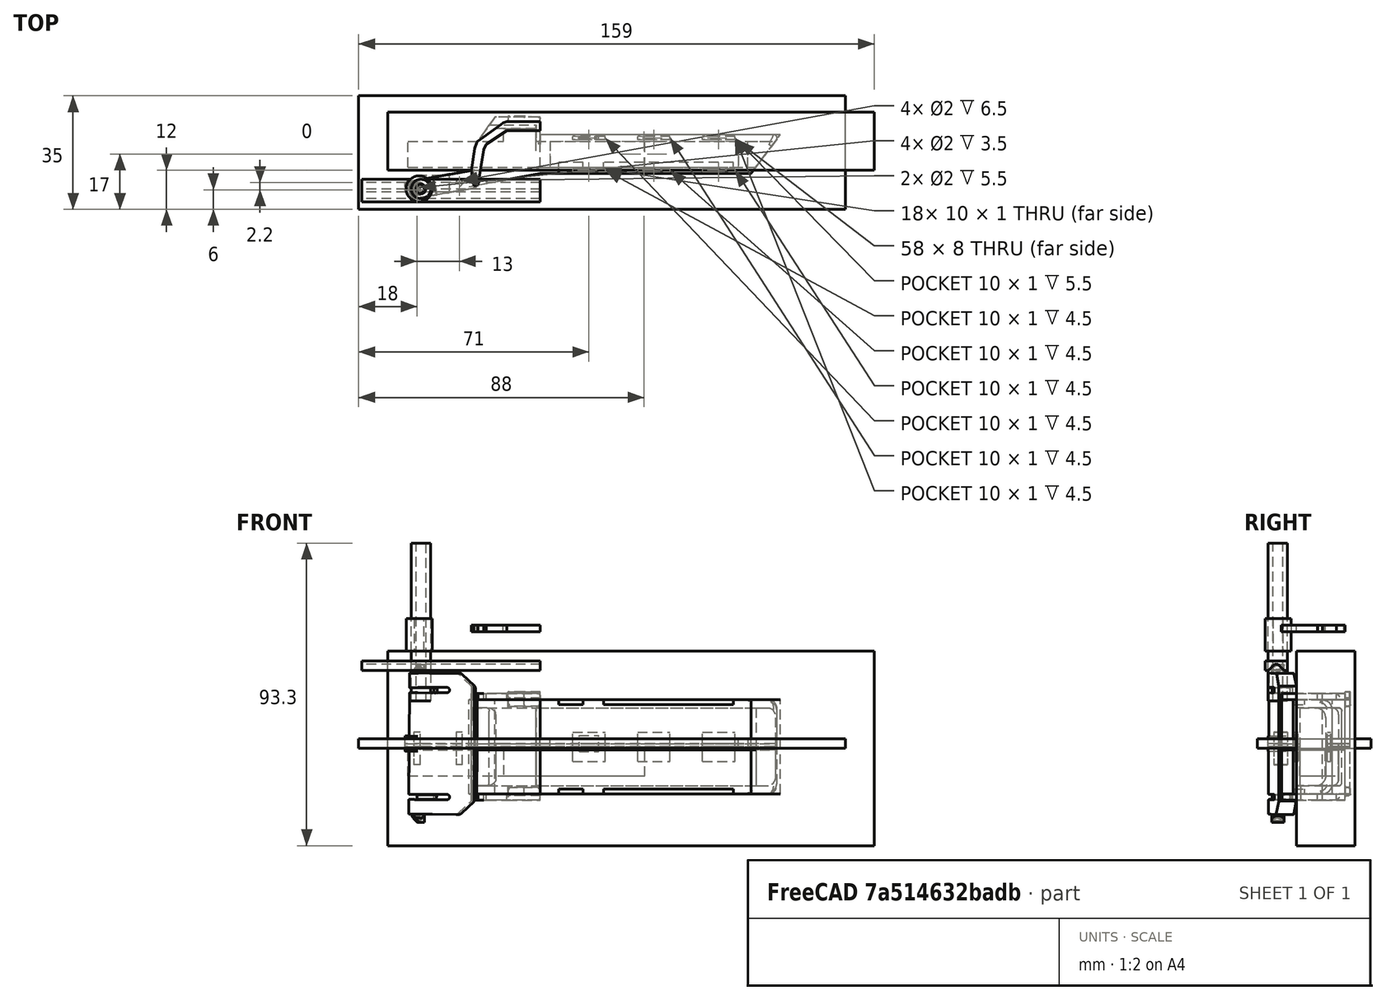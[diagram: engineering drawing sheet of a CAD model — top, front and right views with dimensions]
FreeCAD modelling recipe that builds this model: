
FCSTD DOCUMENT  (FreeCAD 0.21R33771 (Git))
Label: pieza_aspiradora
License: All rights reserved
LicenseURL: http://en.wikipedia.org/wiki/All_rights_reserved
objects: Part::Cut×69, Part::Box×57, Part::Fillet×31, Part::Feature×29, Part::Cylinder×14, Mesh::Feature×10, Sketcher::SketchObject×5, PartDesign::Pad×5, PartDesign::Body×5, Part::Chamfer×4, Part::MultiFuse×4, PartDesign::ShapeBinder×1, Part::Fuse×1
note: 230 computed .brp shape members not serialized (recipe doc carries the construction recipe); baked Part::Feature solids carry a one-line shape summary decoded from their .brp

FEATURE [Sketcher::SketchObject] Sketch
  FullyConstrained = true
  MapMode = 5
  sketch-geometry (8):
    g0: LineSegment StartX=0 StartY=0 StartZ=0 EndX=0 EndY=5.5 EndZ=0
    g1: LineSegment StartX=0 StartY=5.5 StartZ=0 EndX=-14 EndY=5.5 EndZ=0
    g2: LineSegment StartX=-14 StartY=5.5 StartZ=0 EndX=-20 EndY=-3 EndZ=0
    g3: LineSegment StartX=-20 StartY=-3 StartZ=0 EndX=-22 EndY=-16 EndZ=0
    g4: LineSegment StartX=-22 StartY=-16 StartZ=0 EndX=0 EndY=-12 EndZ=0
    g5: LineSegment StartX=0 StartY=-12 StartZ=0 EndX=65 EndY=-12 EndZ=0
    g6: LineSegment StartX=65 StartY=-12 StartZ=0 EndX=74 EndY=0 EndZ=0
    g7: LineSegment StartX=74 StartY=0 StartZ=0 EndX=0 EndY=0 EndZ=0
  constraints (24):
    c: PointOnObject(g0,g-1)
    c: PointOnObject(g0,g-2)
    c: Vertical(g0)
    c: Coincident(g0,g1)
    c: Coincident(g1,g2)
    c: Coincident(g2,g3)
    c: Coincident(g3,g4)
    c: Coincident(g4,g5)
    c: Horizontal(g5)
    c: Coincident(g5,g6)
    c: PointOnObject(g6,g-1)
    c: Coincident(g6,g7)
    c: Coincident(g7,g0)
    c: DistanceX(g7,g7) = 74
    c: DistanceX(g0,g4) = 0
    c: DistanceY(g0,g0) = 5.5
    c: Horizontal(g1)
    c: DistanceX(g1,g1) = 14
    c: DistanceX(g3,g-1) = 22
    c: DistanceX(g2,g0) = 20
    c: DistanceY(g3,g2) = 13
    c: DistanceX(g5,g5) = 65
    c: DistanceY(g5,g6) = 12
    c: DistanceY(g3,g4) = 4
FEATURE [PartDesign::Pad] Pad
  Direction = (0,0,1)
  Length = 29
  Length2 = 10
  Profile = -> Sketch
  ReferenceAxis = -> Sketch [N_Axis]
  Type = 0
FEATURE [Part::Feature] Body001
  shape: bbox 96 x 21.5 x 29 mm, 10 faces (baked)
FEATURE [Part::Fillet] Fillet
  Base = -> Body001
  Edges = 1 edges r=5: [Edge8]
FEATURE [Part::Fillet] Fillet001
  Base = -> Fillet
  Edges = 1 edges r=1: [Edge2]
FEATURE [Part::Fillet] Fillet002
  Base = -> Fillet001
  Edges = 1 edges r=3: [Edge22]
FEATURE [Part::Fillet] Fillet003
  Base = -> Fillet002
  Edges = 1 edges r=3: [Edge34]
FEATURE [Part::Fillet] Fillet004
  Base = -> Fillet003
  Edges = 6 edges r=1: [Edge1,Edge2,Edge3,Edge4,Edge5,Edge6]
FEATURE [Part::Box] Box  label="Cube"
  AttacherType = Attacher::AttachEngine3D
  Height = 24
  Length = 156
  Width = 8
FEATURE [Part::Fillet] Fillet005
  Base = -> Box
  Edges = 2 edges r=3: [Edge11,Edge12]
  Placement = pos=(-30,-10,2.5) rot=(0,0,1;0rad)
FEATURE [Part::Box] Box001  label="Cube001"
  AttacherType = Attacher::AttachEngine3D
  Height = 24
  Length = 28
  Placement = pos=(-29.3,-11,2.5) rot=(0,0,1;0rad)
  Width = 14
FEATURE [Part::Cut] Cut
  Base = -> Fillet004
  Tool = -> Fillet005
FEATURE [Part::Cut] Cut001
  Base = -> Cut
  Tool = -> Box001
FEATURE [Part::Chamfer] Chamfer
  Base = -> Cut001
  Edges = 1 edges r=0.95: [Edge38]
FEATURE [Part::Fillet] Fillet006
  Base = -> Chamfer
  Edges = 2 edges r=1: [Edge63,Edge91]
FEATURE [Part::Box] Box002  label="Cube002"
  AttacherType = Attacher::AttachEngine3D
  Height = 10
  Length = 40
  Placement = pos=(19.5,-12,-8.5) rot=(0,0,1;0rad)
  Width = 3.5
FEATURE [Part::Box] Box003  label="Cube003"
  AttacherType = Attacher::AttachEngine3D
  Height = 10
  Length = 40
  Placement = pos=(19.5,-12,27.5) rot=(0,0,1;0rad)
  Width = 3.5
FEATURE [Part::Box] Box005  label="Cube005"
  AttacherType = Attacher::AttachEngine3D
  Height = 10
  Length = 7.4
  Placement = pos=(5.7,-12,27.5) rot=(0,0,1;0rad)
  Width = 3.5
FEATURE [Part::Cut] Cut002
  Base = -> Fillet006
  Tool = -> Box002
FEATURE [Part::Cut] Cut003
  Base = -> Cut002
  Tool = -> Box003
FEATURE [Part::Box] Box006  label="Cube006"
  AttacherType = Attacher::AttachEngine3D
  Height = 10
  Length = 7.4
  Placement = pos=(5.7,-12,-8.5) rot=(0,0,1;0rad)
  Width = 3.5
FEATURE [Part::Cut] Cut004
  Base = -> Cut003
  Tool = -> Box005
FEATURE [Part::Cut] Cut005
  Base = -> Cut004
  Tool = -> Box006
FEATURE [Part::Box] Box007  label="Cube007"
  AttacherType = Attacher::AttachEngine3D
  Height = 30
  Length = 133
  Placement = pos=(-51,-22,14.5) rot=(0,0,1;0rad)
  Width = 30
FEATURE [Part::Box] Box008  label="Cube008"
  AttacherType = Attacher::AttachEngine3D
  Height = 30
  Length = 133
  Placement = pos=(-51,-22,-15.5) rot=(0,0,1;0rad)
  Width = 30
FEATURE [Part::Feature] Fillet003004001  label="pieza2_solida2"
  Placement = pos=(-31.9,-18.5,15.45) rot=(-0.059649,0.705848,0.705848;3.26865rad)
  shape: bbox 21.78 x 8.705 x 48.62 mm, 40 faces (baked)
FEATURE [Part::MultiFuse] Fusion
  Refine = true
  Shapes = -> [Cut005,Fillet003004001]
FEATURE [Part::Feature] Fusion001
  shape: bbox 114.9 x 25.2 x 48.62 mm, 92 faces (baked)
FEATURE [Part::Feature] Fusion002
  shape: bbox 114.9 x 25.2 x 48.62 mm, 92 faces (baked)
FEATURE [Part::Cut] Cut006
  Base = -> Fusion001
  Refine = true
  Tool = -> Box007
FEATURE [Part::Cut] Cut007
  Base = -> Fusion002
  Refine = true
  Tool = -> Box008
FEATURE [Part::Chamfer] Chamfer001  label="mitad1"
  Base = -> Cut006
  Edges = 1 edges r=0.72: [Edge121]
FEATURE [Part::Chamfer] Chamfer002  label="mitad2"
  Base = -> Cut007
  Edges = 1 edges r=0.72: [Edge127]
FEATURE [Part::Chamfer] Chamfer003  label="entera"
  Base = -> Fusion
  Edges = 1 edges r=0.72: [Edge141]
FEATURE [Part::Fillet] Fillet003004002  label="entire_solid2"
  Base = -> Chamfer003
  Edges = 4 edges r=0.7: [Edge20,Edge21,Edge46,Edge47]
FEATURE [Part::Fillet] Fillet003004003
  Base = -> Chamfer002
  Edges = 2 edges r=0.7: [Edge20,Edge21]
FEATURE [Part::Fillet] Fillet003004004
  Base = -> Chamfer001
  Edges = 2 edges r=0.7: [Edge20,Edge21]
FEATURE [Part::Box] Box009  label="Cube009"
  AttacherType = Attacher::AttachEngine3D
  Height = 9
  Length = 10
  Placement = pos=(30,-1.5,10) rot=(0,0,1;0rad)
  Width = 1
FEATURE [Part::Box] Box010  label="Cube010"
  AttacherType = Attacher::AttachEngine3D
  Height = 9
  Length = 10
  Placement = pos=(30,-1.5,10) rot=(0,0,1;0rad)
  Width = 1
FEATURE [Part::Box] Box011  label="Cube011"
  AttacherType = Attacher::AttachEngine3D
  Height = 9
  Length = 10
  Placement = pos=(10,-1.5,10) rot=(0,0,1;0rad)
  Width = 1
FEATURE [Part::Box] Box012  label="Cube012"
  AttacherType = Attacher::AttachEngine3D
  Height = 9
  Length = 10
  Placement = pos=(10,-11.5,10) rot=(0,0,1;0rad)
  Width = 1
FEATURE [Part::Box] Box013  label="Cube013"
  AttacherType = Attacher::AttachEngine3D
  Height = 9
  Length = 10
  Placement = pos=(30,-11.5,10) rot=(0,0,1;0rad)
  Width = 1
FEATURE [Part::Box] Box014  label="Cube014"
  AttacherType = Attacher::AttachEngine3D
  Height = 9
  Length = 10
  Placement = pos=(50,-11.5,10) rot=(0,0,1;0rad)
  Width = 1
FEATURE [Part::Feature] Fillet003004002001  label="entire"
  shape: bbox 114.9 x 25.2 x 48.62 mm, 97 faces (baked)
FEATURE [Part::Feature] Fillet003004003001  label="left2"
  shape: bbox 114.9 x 25.2 x 25.31 mm, 64 faces (baked)
FEATURE [Part::Feature] Fillet003004004001  label="right2"
  shape: bbox 114.9 x 25.2 x 23.35 mm, 62 faces (baked)
FEATURE [Part::Box] Box027  label="Cube027"
  AttacherType = Attacher::AttachEngine3D
  Height = 30
  Length = 133
  Placement = pos=(-51,-22,-14.5) rot=(0,0,1;0rad)
  Width = 30
FEATURE [Part::Box] Box028  label="Cube028"
  AttacherType = Attacher::AttachEngine3D
  Height = 30
  Length = 133
  Placement = pos=(-51,-22,15.5) rot=(0,0,1;0rad)
  Width = 30
FEATURE [Part::Feature] Cut013001  label="for_left_holes"
  shape: bbox 114.9 x 25.2 x 48.62 mm, 131 faces (baked)
FEATURE [Part::Feature] Cut013002  label="for_right_holes"
  shape: bbox 114.9 x 25.2 x 48.62 mm, 131 faces (baked)
FEATURE [Part::Cut] Cut013003  label="right_holes_2"
  Base = -> Cut013002
  Refine = true
  Tool = -> Box027
FEATURE [Part::Cylinder] Cylinder
  Angle = 360
  AttacherType = Attacher::AttachEngine3D
  FirstAngle = 0
  Height = 10
  Placement = pos=(-38,-17,9) rot=(0,0,1;0rad)
  Radius = 1
  SecondAngle = 0
FEATURE [Part::Cylinder] Cylinder001
  Angle = 360
  AttacherType = Attacher::AttachEngine3D
  FirstAngle = 0
  Height = 10
  Placement = pos=(-25,-14.8,9) rot=(0,0,1;0rad)
  Radius = 1
  SecondAngle = 0
FEATURE [Part::Cylinder] Cylinder002
  Angle = 360
  AttacherType = Attacher::AttachEngine3D
  FirstAngle = 0
  Height = 10
  Placement = pos=(-38,-17,9) rot=(0,0,1;0rad)
  Radius = 1
  SecondAngle = 0
FEATURE [Part::Cylinder] Cylinder003
  Angle = 360
  AttacherType = Attacher::AttachEngine3D
  FirstAngle = 0
  Height = 10
  Placement = pos=(-25,-14.8,9) rot=(0,0,1;0rad)
  Radius = 1
  SecondAngle = 0
FEATURE [Part::Cylinder] Cylinder004
  Angle = 360
  AttacherType = Attacher::AttachEngine3D
  FirstAngle = 0
  Height = 10
  Placement = pos=(-38,-17,9) rot=(0,0,1;0rad)
  Radius = 1
  SecondAngle = 0
FEATURE [Part::Cylinder] Cylinder005
  Angle = 360
  AttacherType = Attacher::AttachEngine3D
  FirstAngle = 0
  Height = 10
  Placement = pos=(-25,-14.8,9) rot=(0,0,1;0rad)
  Radius = 1
  SecondAngle = 0
FEATURE [Part::Cut] Cut013007
  Base = -> Cut013003
  Refine = true
  Tool = -> Cylinder002
FEATURE [Part::Cut] Cut013008  label="right_holes"
  Base = -> Cut013007
  Refine = true
  Tool = -> Cylinder003
FEATURE [Part::Feature] Fillet003004002002  label="entire_test_1"
  shape: bbox 114.9 x 25.2 x 48.62 mm, 97 faces (baked)
FEATURE [Part::Feature] Fillet003004004002  label="entire_test_2"
  shape: bbox 114.9 x 25.2 x 48.62 mm, 97 faces (baked)
FEATURE [Part::Feature] Fillet003004004003  label="entire_test_3"
  shape: bbox 114.9 x 25.2 x 48.62 mm, 97 faces (baked)
FEATURE [Part::Cut] Cut013009
  Base = -> Cut013001
  Refine = true
  Tool = -> Box028
FEATURE [Part::Cut] Cut013010
  Base = -> Cut013009
  Refine = true
  Tool = -> Cylinder001
FEATURE [Part::Cut] Cut013011  label="left_holes"
  Base = -> Cut013010
  Refine = true
  Tool = -> Cylinder
FEATURE [Part::Box] Box029  label="Cube029"
  AttacherType = Attacher::AttachEngine3D
  Height = 60
  Length = 150
  Placement = pos=(-47,-11,-16) rot=(0,0,1;0rad)
  Width = 18
FEATURE [Part::Box] Box030  label="Cube030"
  AttacherType = Attacher::AttachEngine3D
  Height = 25
  Length = 150
  Placement = pos=(-56,-23,-11) rot=(0,0,1;0rad)
  Width = 35
FEATURE [Part::Box] Box031  label="Cube031"
  AttacherType = Attacher::AttachEngine3D
  Height = 25
  Length = 150
  Placement = pos=(-56,-23,17) rot=(0,0,1;0rad)
  Width = 35
FEATURE [Part::Box] Box032  label="Cube032"
  AttacherType = Attacher::AttachEngine3D
  Height = 3
  Length = 64
  Placement = pos=(0,-12,14) rot=(0,0,1;0rad)
  Width = 12
FEATURE [Part::Box] Box033  label="Cube033"
  AttacherType = Attacher::AttachEngine3D
  Height = 3
  Length = 150
  Placement = pos=(-56,-23,14) rot=(0,0,1;0rad)
  Width = 35
FEATURE [Part::MultiFuse] Fusion003
  Refine = true
  Shapes = -> [Fillet003004002002,Box032]
FEATURE [Part::Cut] Cut013012
  Base = -> Fusion003
  Refine = true
  Tool = -> Box030
FEATURE [Part::Cut] Cut013013
  Base = -> Cut013012
  Refine = true
  Tool = -> Box031
FEATURE [Part::Box] Box034  label="Cube034"
  AttacherType = Attacher::AttachEngine3D
  Height = 10
  Length = 58
  Placement = pos=(3,-10,10) rot=(0,0,1;0rad)
  Width = 8
FEATURE [Part::Cut] Cut013014  label="for_test"
  Base = -> Cut013013
  Refine = true
  Tool = -> Box034
FEATURE [Mesh::Feature] Mesh003  label="for_test (Meshed)"
FEATURE [Part::Feature] Cut013014001  label="for_test001"
  shape: bbox 114.8 x 25.2 x 3.03 mm, 36 faces (baked)
FEATURE [Part::Feature] Cut005006002  label="cortador_15"
  Placement = pos=(-42,-14,53) rot=(1,0,0;1.5708rad)
  shape: bbox 6 x 6 x 48.6 mm, 4 faces (baked)
FEATURE [Part::Cylinder] Cylinder006
  Angle = 360
  AttacherType = Attacher::AttachEngine3D
  FirstAngle = 0
  Height = 10
  Placement = pos=(-37.37,-16.69,44) rot=(0,0,1;0rad)
  Radius = 1.5
  SecondAngle = 0
FEATURE [Part::Cylinder] Cylinder007
  Angle = 360
  AttacherType = Attacher::AttachEngine3D
  FirstAngle = 0
  Height = 10
  Placement = pos=(-37.37,-16.69,44) rot=(0,0,1;0rad)
  Radius = 4
  SecondAngle = 0
FEATURE [Part::Cut] Cut013014002
  Base = -> Cylinder007
  Tool = -> Cylinder006
FEATURE [Part::Feature] Cut013014002001
  Placement = pos=(0,0,-6.8) rot=(0,0,1;0rad)
  shape: bbox 8 x 8 x 10 mm, 4 faces (baked)
FEATURE [Part::Feature] Cut013014002002
  Placement = pos=(0,0,-60.27) rot=(0,0,1;0rad)
  shape: bbox 8 x 8 x 10 mm, 4 faces (baked)
FEATURE [Part::Feature] Cut013014002003
  Placement = pos=(0,0,-6.8) rot=(0,0,1;0rad)
  shape: bbox 8 x 8 x 10 mm, 4 faces (baked)
FEATURE [Part::Feature] Cut013014002004
  Placement = pos=(0,0,-60.27) rot=(0,0,1;0rad)
  shape: bbox 8 x 8 x 10 mm, 4 faces (baked)
FEATURE [Part::Cut] Cut013014002005
  Base = -> Fillet003004002
  Tool = -> Cut013014002001
FEATURE [Part::Cut] Cut013014002006  label="entire_solid_final"
  Base = -> Cut013014002005
  Tool = -> Cut013014002002
FEATURE [Part::Cut] Cut013014002007  label="left5"
  Base = -> Fillet003004003001
  Tool = -> Cut013014002003
FEATURE [Part::Cut] Cut013014002008  label="right5"
  Base = -> Fillet003004004001
  Tool = -> Cut013014002004
FEATURE [Part::Cylinder] Cylinder008
  Angle = 360
  AttacherType = Attacher::AttachEngine3D
  FirstAngle = 0
  Height = 10
  Placement = pos=(-38,-17,9) rot=(0,0,1;0rad)
  Radius = 1
  SecondAngle = 0
FEATURE [Part::Cylinder] Cylinder009
  Angle = 360
  AttacherType = Attacher::AttachEngine3D
  FirstAngle = 0
  Height = 10
  Placement = pos=(-25,-14.8,9) rot=(0,0,1;0rad)
  Radius = 1
  SecondAngle = 0
FEATURE [Part::Cut] Cut013014002009
  Base = -> Cut013014002008
  Tool = -> Cylinder004
FEATURE [Part::Cut] Cut013014002010  label="right6"
  Base = -> Cut013014002009
  Tool = -> Cylinder005
FEATURE [Part::Cut] Cut013014002011
  Base = -> Cut013014002007
  Tool = -> Cylinder008
FEATURE [Part::Cut] Cut013014002012  label="left6"
  Base = -> Cut013014002011
  Tool = -> Cylinder009
FEATURE [Part::Box] Box035  label="Cube035"
  AttacherType = Attacher::AttachEngine3D
  Height = 9
  Length = 10
  Placement = pos=(50,-1.5,10) rot=(0,0,1;0rad)
  Width = 1
FEATURE [Part::Box] Box036  label="Cube036"
  AttacherType = Attacher::AttachEngine3D
  Height = 9
  Length = 10
  Placement = pos=(10,-1.5,10) rot=(0,0,1;0rad)
  Width = 1
FEATURE [Part::Box] Box037  label="Cube037"
  AttacherType = Attacher::AttachEngine3D
  Height = 9
  Length = 10
  Placement = pos=(10,-11.5,10) rot=(0,0,1;0rad)
  Width = 1
FEATURE [Part::Box] Box038  label="Cube038"
  AttacherType = Attacher::AttachEngine3D
  Height = 9
  Length = 10
  Placement = pos=(30,-11.5,10) rot=(0,0,1;0rad)
  Width = 1
FEATURE [Part::Box] Box039  label="Cube039"
  AttacherType = Attacher::AttachEngine3D
  Height = 9
  Length = 10
  Placement = pos=(50,-11.5,10) rot=(0,0,1;0rad)
  Width = 1
FEATURE [Part::Box] Box040  label="Cube040"
  AttacherType = Attacher::AttachEngine3D
  Height = 9
  Length = 10
  Placement = pos=(50,-1.5,10) rot=(0,0,1;0rad)
  Width = 1
FEATURE [Part::Cut] Cut013014002013
  Base = -> Cut013014002012
  Tool = -> Box035
FEATURE [Part::Cut] Cut013014002014
  Base = -> Cut013014002013
  Tool = -> Box010
FEATURE [Part::Cut] Cut013014002015
  Base = -> Cut013014002014
  Tool = -> Box011
FEATURE [Part::Cut] Cut013014002016
  Base = -> Cut013014002015
  Tool = -> Box012
FEATURE [Part::Cut] Cut013014002017
  Base = -> Cut013014002016
  Tool = -> Box013
FEATURE [Part::Cut] Cut013014002018  label="left_final1"
  Base = -> Cut013014002017
  Tool = -> Box014
FEATURE [Part::Cut] Cut013014002019
  Base = -> Cut013014002010
  Tool = -> Box009
FEATURE [Part::Cut] Cut013014002020
  Base = -> Cut013014002019
  Tool = -> Box040
FEATURE [Part::Cut] Cut013014002021
  Base = -> Cut013014002020
  Tool = -> Box039
FEATURE [Part::Cut] Cut013014002022
  Base = -> Cut013014002021
  Tool = -> Box038
FEATURE [Part::Cut] Cut013014002023
  Base = -> Cut013014002022
  Tool = -> Box037
FEATURE [Part::Cut] Cut013014002024  label="right_final1"
  Base = -> Cut013014002023
  Tool = -> Box036
FEATURE [Mesh::Feature] Mesh  label="entire_solid_final (Meshed)"
FEATURE [Mesh::Feature] Mesh004  label="left_final1 (Meshed)"
FEATURE [Mesh::Feature] Mesh005  label="right_final1 (Meshed)"
FEATURE [Part::Box] Box041  label="uniones_planas"
  AttacherType = Attacher::AttachEngine3D
  Height = 5
  Length = 6
  Placement = pos=(12,-1.3,13) rot=(0,0,1;0rad)
  Width = 0.8
FEATURE [PartDesign::ShapeBinder] CopyFillet003004002001
  TraceSupport = false
FEATURE [PartDesign::Body] Body
  Group = -> [Sketch,Pad,CopyFillet003004002001]
  Origin = -> Origin
  Tip = -> Pad
FEATURE [Sketcher::SketchObject] Sketch001
  ExternalGeometry = -> [Fillet003004002001]
  FullyConstrained = true
  MapMode = 5
  sketch-geometry (6):
    g0: LineSegment StartX=2.6782 StartY=7.46078 StartZ=0 EndX=2.6782 EndY=4 EndZ=0
    g1: LineSegment StartX=2.6782 StartY=4 StartZ=0 EndX=-10.9318 EndY=4 EndZ=0
    g2: LineSegment StartX=-10.9318 StartY=4 StartZ=0 EndX=-19.3218 EndY=-2.03922 EndZ=0
    g3: LineSegment StartX=-19.3218 StartY=-2.03922 StartZ=0 EndX=-22.3218 EndY=-2.03922 EndZ=0
    g4: LineSegment StartX=-22.3218 StartY=-2.03922 StartZ=0 EndX=-22.3218 EndY=7.46078 EndZ=0
    g5: LineSegment StartX=-22.3218 StartY=7.46078 StartZ=0 EndX=2.6782 EndY=7.46078 EndZ=0
  constraints (17):
    c: Vertical(g0)
    c: Coincident(g0,g1)
    c: Horizontal(g1)
    c: Coincident(g1,g2)
    c: Coincident(g2,g3)
    c: Horizontal(g3)
    c: Coincident(g3,g4)
    c: Vertical(g4)
    c: Coincident(g4,g5)
    c: Coincident(g5,g0)
    c: Horizontal(g5)
    c: DistanceY(g0,g-3) = 1.5
    c: DistanceX(g-3,g1) = 2.55
    c: DistanceX(g5,g5) = 25
    c: DistanceX(g3,g3) = 3
    c: Coincident(g2,g-4)
    c: DistanceY(g4,g4) = 9.5
FEATURE [PartDesign::Pad] Pad001
  Direction = (0,0,1)
  Length = 98
  Length2 = 10
  Midplane = true
  Profile = -> Sketch001
  ReferenceAxis = -> Sketch001 [N_Axis]
  Type = 0
FEATURE [PartDesign::Body] Body002
  Group = -> [Sketch001,Pad001]
  Origin = -> Origin001
  Tip = -> Pad001
FEATURE [Part::Box] Box042  label="Cube041"
  AttacherType = Attacher::AttachEngine3D
  Height = 29
  Length = 18
  Placement = pos=(-18,2,0) rot=(0,0,1;0rad)
  Width = 1
FEATURE [Part::MultiFuse] Fusion004
  Shapes = -> [Fillet003004002001,Box042]
FEATURE [Part::Cut] Cut013014002025
  Base = -> Fusion004
  Tool = -> Body002
FEATURE [Part::Fillet] Fillet003004004004
  Base = -> Cut013014002025
  Edges = 2 edges r=2: [Edge1,Edge3]
FEATURE [Part::Fillet] Fillet003004004005  label="pieza_perfilada_v2"
  Base = -> Fillet003004004004
  Edges = 1 edges r=2: [Edge21]
FEATURE [Part::Box] Box043  label="Cube042"
  AttacherType = Attacher::AttachEngine3D
  Height = 10
  Length = 10
  Placement = pos=(-42.75,-25,-14) rot=(0,1,0;0.785398rad)
  Width = 30
FEATURE [Part::Box] Box044  label="Cube043"
  AttacherType = Attacher::AttachEngine3D
  Height = 10
  Length = 10
  Placement = pos=(-42.5,-25,44.9) rot=(0,1,0;0.785398rad)
  Width = 30
FEATURE [Part::Cut] Cut013014002026
  Base = -> Fillet003004004005
  Tool = -> Box043
FEATURE [Part::Cut] Cut013014002027
  Base = -> Cut013014002026
  Tool = -> Box044
FEATURE [Part::Box] Box045  label="Cube044"
  AttacherType = Attacher::AttachEngine3D
  Height = 10
  Length = 10
  Placement = pos=(-44,-22,39.4) rot=(0,0,1;0rad)
  Width = 10
FEATURE [Part::Box] Box046  label="Cube045"
  AttacherType = Attacher::AttachEngine3D
  Height = 10
  Length = 10
  Placement = pos=(-44,-22,-18.3) rot=(0,0,1;0rad)
  Width = 10
FEATURE [Part::Cut] Cut013014002028
  Base = -> Cut013014002027
  Tool = -> Box045
FEATURE [Part::Cut] Cut013014002029
  Base = -> Cut013014002028
  Tool = -> Box046
FEATURE [Part::Fillet] Fillet003004004006
  Base = -> Cut013014002029
  Edges = 2 edges r=0.7: [Edge299,Edge300]
FEATURE [Part::Fillet] Fillet003004004007
  Base = -> Fillet003004004006
  Edges = 2 edges r=0.4: [Edge274,Edge275]
FEATURE [Sketcher::SketchObject] Sketch002
  FullyConstrained = false
  MapMode = 5
  Placement = pos=(0,0,0) rot=(0.57735,0.57735,0.57735;2.0944rad)
  sketch-geometry (9):
    g0: LineSegment StartX=-19.6578 StartY=37.9917 StartZ=0 EndX=-17.7211 EndY=39.9284 EndZ=0
    g1: LineSegment StartX=-17.7211 StartY=39.9284 StartZ=0 EndX=-16.7211 EndY=39.9284 EndZ=0
    g2: LineSegment StartX=-16.7211 StartY=39.9284 StartZ=0 EndX=-14.7845 EndY=37.9917 EndZ=0
    g3: LineSegment StartX=-14.7845 StartY=37.9917 StartZ=0 EndX=-13.7845 EndY=37.9917 EndZ=0
    g4: LineSegment StartX=-13.7845 StartY=37.9917 StartZ=0 EndX=-13.7845 EndY=40.9917 EndZ=0
    g5: LineSegment StartX=-13.7845 StartY=40.9917 StartZ=0 EndX=-19.2072 EndY=40.9917 EndZ=0
    g6: LineSegment StartX=-19.6578 StartY=37.9917 StartZ=0 EndX=-20.6578 EndY=37.9917 EndZ=0
    g7: LineSegment StartX=-20.6578 StartY=37.9917 StartZ=0 EndX=-20.6578 EndY=40.9917 EndZ=0
    g8: LineSegment StartX=-20.6578 StartY=40.9917 StartZ=0 EndX=-19.2072 EndY=40.9917 EndZ=0
  constraints (24):
    c: Coincident(g0,g1)
    c: Horizontal(g1)
    c: Coincident(g1,g2)
    c: Coincident(g2,g3)
    c: Horizontal(g3)
    c: Coincident(g3,g4)
    c: Vertical(g4)
    c: Coincident(g4,g5)
    c: Horizontal(g5)
    c: Coincident(g0,g6)
    c: Horizontal(g6)
    c: Coincident(g6,g7)
    c: Vertical(g7)
    c: Coincident(g7,g8)
    c: Coincident(g8,g5)
    c: Horizontal(g8)
    c: Angle(g0,g6) = 2.35619
    c: Angle(g3,g2) = 2.35619
    c: Equal(g1,g6)
    c: Equal(g6,g3)
    c: Equal(g7,g4)
    c: DistanceX(g1,g1) = 1
    c: DistanceX(g6,g6) = 1
    c: DistanceY(g7,g7) = 3
FEATURE [PartDesign::Pad] Pad002
  Direction = (1,0,0)
  Length = 55
  Length2 = 10
  Placement = pos=(0,0,0) rot=(0.57735,0.57735,0.57735;2.0944rad)
  Profile = -> Sketch002
  ReferenceAxis = -> Sketch002 [N_Axis]
  Reversed = true
  Type = 0
FEATURE [PartDesign::Body] Body003
  Group = -> [Sketch002,Pad002]
  Origin = -> Origin002
  Tip = -> Pad002
FEATURE [Part::Feature] Body003001
  Placement = pos=(0,0.3,-0.11) rot=(0,0,1;0rad)
  shape: bbox 55 x 6.873 x 3 mm, 11 faces (baked)
FEATURE [Part::Feature] Body003002
  Placement = pos=(-55,0.3,31.13) rot=(0,1,0;3.14159rad)
  shape: bbox 55 x 6.873 x 3 mm, 11 faces (baked)
FEATURE [Part::Cut] Cut013014002030
  Base = -> Fillet003004004007
  Tool = -> Body003001
FEATURE [Part::Cut] Cut013014002031
  Base = -> Cut013014002030
  Tool = -> Body003002
FEATURE [Part::Fillet] Fillet003004004008
  Base = -> Cut013014002031
  Edges = 4 edges r=0.5: [Edge280,Edge289,Edge290,Edge291]
FEATURE [Part::Fillet] Fillet003004004009
  Base = -> Fillet003004004008
  Edges = 5 edges r=0.5: [Edge13,Edge16,Edge17,Edge18,Edge19]
FEATURE [Part::Fillet] Fillet003004004010
  Base = -> Fillet003004004009
  Edges = 6 edges r=0.5: [Edge223,Edge316,Edge321,Edge323,Edge324,Edge325]
FEATURE [Part::Fillet] Fillet003004004011
  Base = -> Fillet003004004010
  Edges = 6 edges r=0.5: [Edge8,Edge10,Edge17,Edge18,Edge19,Edge20]
FEATURE [Part::Fillet] Fillet003004004012  label="pieza_sin_cuernitos"
  Base = -> Fillet003004004011
  Edges = 1 edges r=0.5: [Edge229]
FEATURE [Sketcher::SketchObject] Sketch003
  FullyConstrained = true
  MapMode = 5
  Placement = pos=(0,0,29) rot=(0,0,1;0rad)
  sketch-geometry (5):
    g0: LineSegment StartX=0 StartY=3.95 StartZ=0 EndX=0 EndY=5.4 EndZ=0
    g1: LineSegment StartX=0 StartY=5.4 StartZ=0 EndX=-5 EndY=5.65 EndZ=0
    g2: LineSegment StartX=-5 StartY=5.65 StartZ=0 EndX=-10 EndY=5.65 EndZ=0
    g3: LineSegment StartX=-10 StartY=5.65 StartZ=0 EndX=-10 EndY=3.95 EndZ=0
    g4: LineSegment StartX=-10 StartY=3.95 StartZ=0 EndX=0 EndY=3.95 EndZ=0
  constraints (15):
    c: PointOnObject(g0,g-2)
    c: PointOnObject(g0,g-2)
    c: Coincident(g0,g1)
    c: Coincident(g1,g2)
    c: Horizontal(g2)
    c: Coincident(g2,g3)
    c: Vertical(g3)
    c: Coincident(g3,g4)
    c: Coincident(g4,g0)
    c: Horizontal(g4)
    c: DistanceX(g2,g2) = 5
    c: DistanceX(g1,g1) = 5
    c: DistanceY(g3,g3) = 1.7
    c: DistanceY(g0,g0) = 1.45
    c: DistanceY(g-1,g0) = 3.95
FEATURE [PartDesign::Pad] Pad003
  Direction = (0,0,1)
  Length = 2.5
  Length2 = 10
  Placement = pos=(0,0,29) rot=(0,0,1;0rad)
  Profile = -> Sketch003
  ReferenceAxis = -> Sketch003 [N_Axis]
  Type = 0
FEATURE [PartDesign::Body] Body003003
  Group = -> [Sketch003,Pad003]
  Origin = -> Origin003
  Tip = -> Pad003
FEATURE [Part::Feature] Fillet003004004013001  label="cuerno1"
  Placement = pos=(0,0,-2) rot=(0,0,1;0rad)
  shape: bbox 10.02 x 1.7 x 2.5 mm, 13 faces (baked)
FEATURE [Part::Feature] Fillet003004004013002  label="cuerno2"
  Placement = pos=(0,0,-29.5) rot=(0,0,1;0rad)
  shape: bbox 10.02 x 1.7 x 2.5 mm, 13 faces (baked)
FEATURE [Sketcher::SketchObject] Sketch004
  FullyConstrained = false
  MapMode = 5
  Placement = pos=(0,0,29) rot=(0,0,1;0rad)
  sketch-geometry (15):
    g0: LineSegment StartX=-19.1871 StartY=-15.4726 StartZ=0 EndX=-17.5094 EndY=-4.56759 EndZ=0
    g1: LineSegment StartX=-17.5094 StartY=-4.56759 StartZ=0 EndX=-16.6218 EndY=-2.97871 EndZ=0
    g2: LineSegment StartX=-16.6218 StartY=-2.97871 StartZ=0 EndX=-10.2869 EndY=1.3 EndZ=0
    g3: LineSegment StartX=-10.2869 StartY=1.3 StartZ=0 EndX=0 EndY=1.3 EndZ=0
    g4: LineSegment StartX=0 StartY=1.3 StartZ=0 EndX=0 EndY=4 EndZ=0
    g5: LineSegment StartX=0 StartY=4 StartZ=0 EndX=-10.2869 EndY=4 EndZ=0
    g6: LineSegment StartX=-10.2869 StartY=4 StartZ=0 EndX=-11.4553 EndY=3.62321 EndZ=0
    g7: LineSegment StartX=-11.4553 StartY=3.62321 StartZ=0 EndX=-12.0956 EndY=3.16232 EndZ=0
    g8: LineSegment StartX=-12.0956 StartY=3.16232 StartZ=0 EndX=-13.4848 EndY=2.16232 EndZ=0
    g9: LineSegment StartX=-13.4848 StartY=2.16232 StartZ=0 EndX=-19.3218 EndY=-2.03922 EndZ=0
    g10: LineSegment StartX=-19.3218 StartY=-2.03922 StartZ=0 EndX=-19.605 EndY=-2.48951 EndZ=0
    g11: LineSegment StartX=-19.605 StartY=-2.48951 StartZ=0 EndX=-20.1788 EndY=-4.16235 EndZ=0
    g12: LineSegment StartX=-20.1788 StartY=-4.16235 StartZ=0 EndX=-21.2378 EndY=-11.0459 EndZ=0
    g13: LineSegment StartX=-21.2378 StartY=-11.0459 StartZ=0 EndX=-20.5503 EndY=-15.7241 EndZ=0
    g14: LineSegment StartX=-20.5503 StartY=-15.7241 StartZ=0 EndX=-19.1871 EndY=-15.4726 EndZ=0
  constraints (18):
    c: Coincident(g0,g1)
    c: Coincident(g1,g2)
    c: Coincident(g2,g3)
    c: Horizontal(g3)
    c: Distance(g1) = 1.82
    c: Vertical(g3,g-1)
    c: Coincident(g3,g4)
    c: Coincident(g4,g5)
    c: Coincident(g5,g6)
    c: Coincident(g6,g7)
    c: Coincident(g7,g8)
    c: Coincident(g8,g9)
    c: Coincident(g9,g10)
    c: Coincident(g10,g11)
    c: Coincident(g11,g12)
    c: Coincident(g12,g13)
    c: Coincident(g13,g14)
    c: Coincident(g14,g0)
FEATURE [PartDesign::Pad] Pad004
  Direction = (0,0,1)
  Length = 2
  Length2 = 10
  Placement = pos=(0,0,29) rot=(0,0,1;0rad)
  Profile = -> Sketch004
  ReferenceAxis = -> Sketch004 [N_Axis]
  Type = 0
FEATURE [PartDesign::Body] Body003004
  Group = -> [Sketch004,Pad004]
  Origin = -> Origin004
  Placement = pos=(0,0,21) rot=(0,0,1;0rad)
  Tip = -> Pad004
FEATURE [Part::Fillet] Fillet003004004013003
  Base = -> Pad004
  Edges = 5 edges r=0.5: [Edge17,Edge20,Edge29,Edge32,Edge35]
FEATURE [Part::Feature] Fillet003004004013003001  label="borde1"
  shape: bbox 21.24 x 19.72 x 2 mm, 22 faces (baked)
FEATURE [Part::Feature] Fillet003004004013003002  label="borde2"
  Placement = pos=(0,0,-31) rot=(0,0,1;0rad)
  shape: bbox 21.24 x 19.72 x 2 mm, 22 faces (baked)
FEATURE [Part::MultiFuse] Fusion005
  Shapes = -> [Fillet003004004013003001,Fillet003004004013003002,Fillet003004004013002,Fillet003004004013001,Fillet003004004012]
FEATURE [Part::Box] Box047  label="Cube046"
  AttacherType = Attacher::AttachEngine3D
  Height = 44
  Length = 11
  Placement = pos=(-20.5,-5,-8) rot=(0,0,1;1.16937rad)
  Width = 16
FEATURE [Part::Cut] Cut013014002032
  Base = -> Fusion005
  Tool = -> Box047
FEATURE [Part::Fillet] Fillet003004004013003003
  Base = -> Cut013014002032
  Edges = 8 edges r=1: [Edge174,Edge175,Edge177,Edge178,Edge315,Edge319,Edge381,Edge393]
FEATURE [Part::Fillet] Fillet003004004013003004
  Base = -> Fillet003004004013003003
  Edges = 4 edges r=0.5: [Edge102,Edge272,Edge273,Edge347]
FEATURE [Part::Fillet] Fillet003004004013003005
  Base = -> Fillet003004004013003004
  Edges = 3 edges r=0.5: [Edge45,Edge137,Edge139]
FEATURE [Part::Fillet] Fillet003004004013003006
  Base = -> Fillet003004004013003005
  Edges = 2 edges r=1: [Edge8,Edge80]
FEATURE [Part::Fillet] Fillet003004004013003007
  Base = -> Fillet003004004013003005
  Edges = 2 edges r=1: [Edge173,Edge362]
FEATURE [Part::Fillet] Fillet003004004013003008
  Base = -> Fillet003004004013003007
  Edges = 3 edges r=0.5: [Edge22,Edge26,Edge33]
FEATURE [Part::Fillet] Fillet003004004013003009  label="pieza_entera_version2"
  Base = -> Fillet003004004013003008
  Edges = 4 edges r=0.5: [Edge16,Edge51,Edge221,Edge390]
FEATURE [Part::Feature] Fillet003004004013003009001  label="pieza_entera_version_21"
  shape: bbox 114.9 x 25.35 x 47.71 mm, 233 faces (baked)
FEATURE [Part::Feature] Fillet003004004013003009002  label="pieza_entera_version_para_mitad1"
  shape: bbox 114.9 x 25.35 x 47.71 mm, 233 faces (baked)
FEATURE [Part::Feature] Fillet003004004013003009003  label="pieza_entera_version_para_mitad2"
  shape: bbox 114.9 x 25.35 x 47.71 mm, 233 faces (baked)
FEATURE [Part::Box] Box048  label="Cube047"
  AttacherType = Attacher::AttachEngine3D
  Height = 30
  Length = 133
  Placement = pos=(-51,-23,-14.5) rot=(0,0,1;0rad)
  Width = 30
FEATURE [Part::Box] Box049  label="Cube048"
  AttacherType = Attacher::AttachEngine3D
  Height = 30
  Length = 133
  Placement = pos=(-51,-23,15.5) rot=(0,0,1;0rad)
  Width = 30
FEATURE [Part::Cylinder] Cylinder010
  Angle = 360
  AttacherType = Attacher::AttachEngine3D
  FirstAngle = 0
  Height = 10
  Placement = pos=(-25,-14.8,9) rot=(0,0,1;0rad)
  Radius = 1
  SecondAngle = 0
FEATURE [Part::Cylinder] Cylinder011
  Angle = 360
  AttacherType = Attacher::AttachEngine3D
  FirstAngle = 0
  Height = 10
  Placement = pos=(-38,-17,9) rot=(0,0,1;0rad)
  Radius = 1
  SecondAngle = 0
FEATURE [Part::Box] Box050  label="Cube049"
  AttacherType = Attacher::AttachEngine3D
  Height = 9
  Length = 10
  Placement = pos=(50,-1.5,10) rot=(0,0,1;0rad)
  Width = 1
FEATURE [Part::Box] Box051  label="Cube050"
  AttacherType = Attacher::AttachEngine3D
  Height = 9
  Length = 10
  Placement = pos=(50,-11.5,10) rot=(0,0,1;0rad)
  Width = 1
FEATURE [Part::Box] Box052  label="Cube051"
  AttacherType = Attacher::AttachEngine3D
  Height = 9
  Length = 10
  Placement = pos=(30,-11.5,10) rot=(0,0,1;0rad)
  Width = 1
FEATURE [Part::Box] Box053  label="Cube052"
  AttacherType = Attacher::AttachEngine3D
  Height = 9
  Length = 10
  Placement = pos=(10,-11.5,10) rot=(0,0,1;0rad)
  Width = 1
FEATURE [Part::Box] Box054  label="Cube053"
  AttacherType = Attacher::AttachEngine3D
  Height = 9
  Length = 10
  Placement = pos=(10,-1.5,10) rot=(0,0,1;0rad)
  Width = 1
FEATURE [Part::Box] Box055  label="Cube054"
  AttacherType = Attacher::AttachEngine3D
  Height = 9
  Length = 10
  Placement = pos=(30,-1.5,10) rot=(0,0,1;0rad)
  Width = 1
FEATURE [Part::Cylinder] Cylinder012
  Angle = 360
  AttacherType = Attacher::AttachEngine3D
  FirstAngle = 0
  Height = 10
  Placement = pos=(-25,-14.8,9) rot=(0,0,1;0rad)
  Radius = 1
  SecondAngle = 0
FEATURE [Part::Cylinder] Cylinder013
  Angle = 360
  AttacherType = Attacher::AttachEngine3D
  FirstAngle = 0
  Height = 10
  Placement = pos=(-38,-17,9) rot=(0,0,1;0rad)
  Radius = 1
  SecondAngle = 0
FEATURE [Part::Box] Box056  label="Cube055"
  AttacherType = Attacher::AttachEngine3D
  Height = 9
  Length = 10
  Placement = pos=(50,-1.5,10) rot=(0,0,1;0rad)
  Width = 1
FEATURE [Part::Box] Box057  label="Cube056"
  AttacherType = Attacher::AttachEngine3D
  Height = 9
  Length = 10
  Placement = pos=(50,-11.5,10) rot=(0,0,1;0rad)
  Width = 1
FEATURE [Part::Box] Box058  label="Cube057"
  AttacherType = Attacher::AttachEngine3D
  Height = 9
  Length = 10
  Placement = pos=(30,-11.5,10) rot=(0,0,1;0rad)
  Width = 1
FEATURE [Part::Box] Box059  label="Cube058"
  AttacherType = Attacher::AttachEngine3D
  Height = 9
  Length = 10
  Placement = pos=(10,-11.5,10) rot=(0,0,1;0rad)
  Width = 1
FEATURE [Part::Box] Box060  label="Cube059"
  AttacherType = Attacher::AttachEngine3D
  Height = 9
  Length = 10
  Placement = pos=(10,-1.5,10) rot=(0,0,1;0rad)
  Width = 1
FEATURE [Part::Box] Box061  label="Cube060"
  AttacherType = Attacher::AttachEngine3D
  Height = 9
  Length = 10
  Placement = pos=(30,-1.5,10) rot=(0,0,1;0rad)
  Width = 1
FEATURE [Part::Cut] Cut013014002051
  Base = -> Fillet003004004013003009002
  Tool = -> Box048
FEATURE [Part::Cut] Cut013014002052
  Base = -> Cut013014002051
  Tool = -> Box061
FEATURE [Part::Cut] Cut013014002053
  Base = -> Cut013014002052
  Tool = -> Box060
FEATURE [Part::Cut] Cut013014002054
  Base = -> Cut013014002053
  Tool = -> Box059
FEATURE [Part::Cut] Cut013014002055
  Base = -> Cut013014002054
  Tool = -> Box058
FEATURE [Part::Cut] Cut013014002056
  Base = -> Cut013014002055
  Tool = -> Box057
FEATURE [Part::Cut] Cut013014002057
  Base = -> Cut013014002056
  Tool = -> Box056
FEATURE [Part::Cut] Cut013014002058
  Base = -> Cut013014002057
  Tool = -> Cylinder013
FEATURE [Part::Cut] Cut013014002059  label="mitad_1_version2_small1"
  Base = -> Cut013014002058
  Tool = -> Cylinder012
FEATURE [Part::Cut] Cut013014002060
  Base = -> Fillet003004004013003009003
  Tool = -> Box049
FEATURE [Part::Cut] Cut013014002061
  Base = -> Cut013014002060
  Tool = -> Box055
FEATURE [Part::Cut] Cut013014002062
  Base = -> Cut013014002061
  Tool = -> Box054
FEATURE [Part::Cut] Cut013014002063
  Base = -> Cut013014002062
  Tool = -> Box053
FEATURE [Part::Cut] Cut013014002064
  Base = -> Cut013014002063
  Tool = -> Box052
FEATURE [Part::Cut] Cut013014002065
  Base = -> Cut013014002064
  Tool = -> Box051
FEATURE [Part::Cut] Cut013014002066
  Base = -> Cut013014002065
  Tool = -> Box050
FEATURE [Part::Cut] Cut013014002067
  Base = -> Cut013014002066
  Tool = -> Cylinder011
FEATURE [Part::Cut] Cut013014002068  label="mitad_2_version_2_big2"
  Base = -> Cut013014002067
  Tool = -> Cylinder010
FEATURE [Part::Box] Box062  label="Cube061"
  AttacherType = Attacher::AttachEngine3D
  Height = 1.6
  Length = 10
  Placement = pos=(-38,-21,-1.8) rot=(0,0,1;0rad)
  Width = 10
FEATURE [Part::Box] Box063  label="Cube062"
  AttacherType = Attacher::AttachEngine3D
  Height = 1.6
  Length = 10
  Placement = pos=(-38,-22,31.2) rot=(0,0,1;0rad)
  Width = 10
FEATURE [Part::Cut] Cut013014002069  label="mitad_2_version_2_big"
  Base = -> Cut013014002068
  Tool = -> Box062
FEATURE [Part::Cut] Cut013014002070  label="mitad_1_version2_small"
  Base = -> Cut013014002059
  Tool = -> Box063
FEATURE [Part::Box] Box064  label="cunia"
  AttacherType = Attacher::AttachEngine3D
  Height = 1.5
  Length = 10
  Placement = pos=(-38,-17.5,-1.75) rot=(0,0,1;0rad)
  Width = 5
FEATURE [Mesh::Feature] Mesh006  label="uniones_planas (Meshed)"
FEATURE [Mesh::Feature] Mesh007  label="cunia (Meshed)"
FEATURE [Part::Fillet] Fillet003004004013003009004  label="mitad_1_version2_small2"
  Base = -> Cut013014002070
  Edges = 2 edges r=0.74: [Edge76,Edge79]
FEATURE [Part::Fillet] Fillet003004004013003009005  label="mitad_2_version_2_big003"
  Base = -> Cut013014002069
  Edges = 2 edges r=0.74: [Edge220,Edge221]
FEATURE [Mesh::Feature] Mesh008  label="mitad_1_version2_small2 (Meshed)"
FEATURE [Mesh::Feature] Mesh009  label="mitad_2_version_2_big003 (Meshed)"
FEATURE [Part::Fillet] Fillet003004004013003009006
  Base = -> Fillet003004004013003009001
  Edges = 2 edges r=1: [Edge156,Edge336]
FEATURE [Part::Fillet] Fillet003004004013003009007  label="pieza_entera_version_2"
  Base = -> Fillet003004004013003009006
  Edges = 4 edges r=0.74: [Edge254,Edge255,Edge277,Edge278]
FEATURE [Part::Feature] Fillet003004004013003009007002  label="pieza_entera_version_023"
  shape: bbox 114.9 x 25.35 x 47.71 mm, 239 faces (baked)
FEATURE [Part::Box] Box065  label="Cube063"
  AttacherType = Attacher::AttachEngine3D
  Height = 56
  Length = 22
  Placement = pos=(-41,-23,-11) rot=(0,0,1;0.174533rad)
  Width = 18
FEATURE [Part::Box] Box067  label="Cube065"
  AttacherType = Attacher::AttachEngine3D
  Height = 56
  Length = 22
  Placement = pos=(-41.5,-23,-11) rot=(0,0,1;0.174533rad)
  Width = 18
FEATURE [Part::Feature] Fillet003004004013003009007003  label="pieza_entera_version_024"
  shape: bbox 114.9 x 25.35 x 47.71 mm, 239 faces (baked)
FEATURE [Part::Cut] Cut013014002072  label="pieza_sin_pie001"
  Base = -> Fillet003004004013003009007003
  Tool = -> Box067
FEATURE [Part::Cut] Cut013014002073  label="pieza_sin_pie"
  Base = -> Fillet003004004013003009007002
  Tool = -> Box065
FEATURE [Part::Box] Box068  label="Cube066"
  AttacherType = Attacher::AttachEngine3D
  Height = 33
  Length = 137
  Placement = pos=(-51,-19,13.5) rot=(0,0,1;0rad)
  Width = 28
FEATURE [Part::Cut] Cut013014002074  label="mitad_sin_pie"
  Base = -> Cut013014002073
  Tool = -> Box068
FEATURE [Mesh::Feature] Mesh010  label="mitad_sin_pie (Meshed)"
FEATURE [Part::Box] Box069  label="Cube067"
  AttacherType = Attacher::AttachEngine3D
  Height = 8
  Length = 73
  Placement = pos=(-40.78,-10,5.5) rot=(0,0,1;0rad)
  Width = 7.9
FEATURE [Part::Box] Box070  label="Cube068"
  AttacherType = Attacher::AttachEngine3D
  Height = 8
  Length = 10
  Placement = pos=(-11.3,-8.1,5.5) rot=(0,0,1;0rad)
  Width = 10
FEATURE [Part::Fuse] Fusion006  label="regla"
  Base = -> Box069
  Tool = -> Box070
FEATURE [Mesh::Feature] Mesh011  label="regla (Meshed)"
